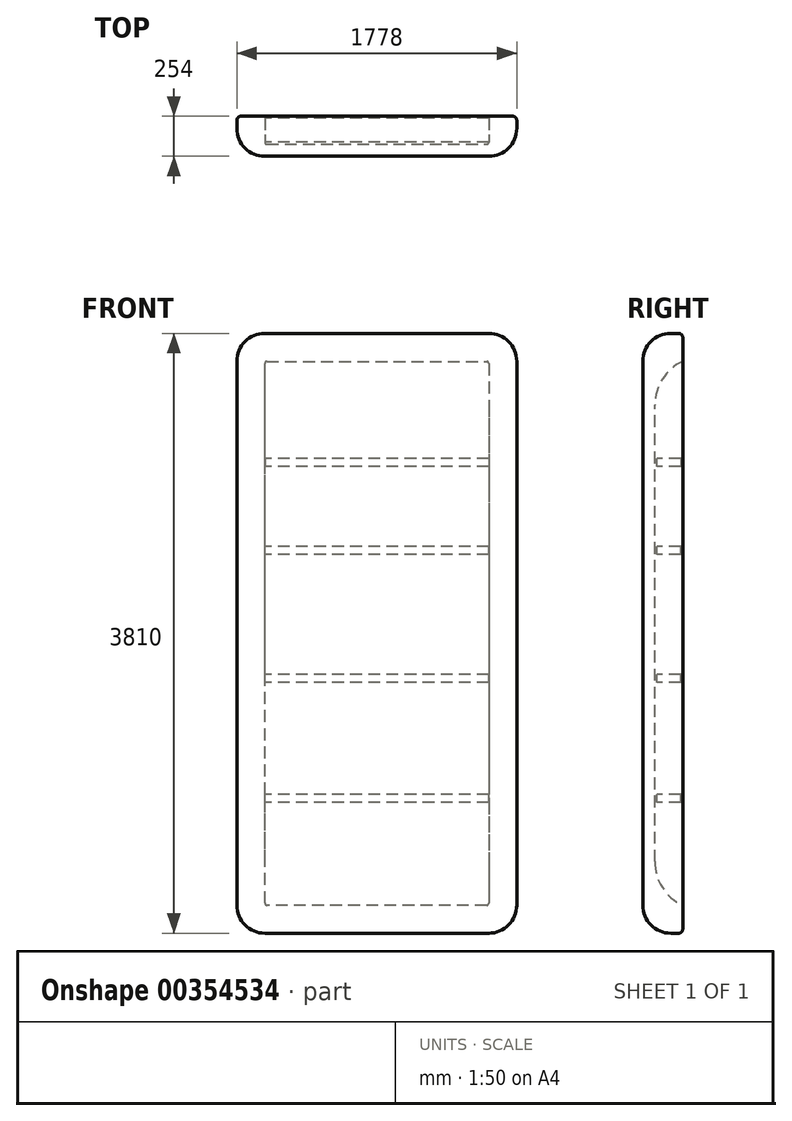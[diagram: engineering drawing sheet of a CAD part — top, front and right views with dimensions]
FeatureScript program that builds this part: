
annotation { "Feature Type Name" : "Feature", "Feature Type Description" : "" }
export const myFeature = defineFeature(function(context is Context, id is Id, definition is map)
    precondition{}
    {
        {
            var Q0;
            Q0=qCreatedBy(makeId("Front.planeOp"),FACE);
            var sketch = newSketch(context, id + "F0", { "sketchPlane" : qUnion([Q0])});
            skLineSegment(sketch, "E0.0", {"start": v(875.3, 1869.2) * mm, "end": v(-902.7, 1869.2) * mm});
            skLineSegment(sketch, "E0.1", {"start": v(875.3, -1940.8) * mm, "end": v(875.3, 1869.2) * mm});
            skLineSegment(sketch, "E0.2", {"start": v(-902.7, -1940.8) * mm, "end": v(875.3, -1940.8) * mm});
            skLineSegment(sketch, "E0.3", {"start": v(-902.7, 1869.2) * mm, "end": v(-902.7, -1940.8) * mm});
            skSolve(sketch);
        }
        {
            var Q0;
            Q0=makeQuery(id+"F0.imprint","IMPRINT",FACE,{"disambiguationData":[TD([[makeQuery(id+"F0.imprint","IMPRINT",EDGE,{"derivedFrom":sQuery(id+"F0.wireOp",EDGE,"E0.0")}),1.0]])]});
            extrude(context, id + "F1", {"entities" : qUnion([Q0]), "depth" : 254 * mm});
        }
        {
            var Q0;
            Q0=makeQuery(id+"F1.opExtrude","CAP_FACE",FACE,{"disambiguationData":[OSD([sQuery(id+"F0.wireOp",EDGE,"E0.0"),sQuery(id+"F0.wireOp",EDGE,"E0.1"),sQuery(id+"F0.wireOp",EDGE,"E0.2"),sQuery(id+"F0.wireOp",EDGE,"E0.3")])],"isStart":true});
            var sketch = newSketch(context, id + "F2", { "sketchPlane" : qUnion([Q0])});
            skLineSegment(sketch, "E1.0", {"start": v(724.9, 1691.4) * mm, "end": v(-697.5, 1691.4) * mm});
            skLineSegment(sketch, "E1.1", {"start": v(724.9, -1763) * mm, "end": v(724.9, 1691.4) * mm});
            skLineSegment(sketch, "E1.2", {"start": v(-697.5, -1763) * mm, "end": v(724.9, -1763) * mm});
            skLineSegment(sketch, "E1.3", {"start": v(-697.5, 1691.4) * mm, "end": v(-697.5, -1763) * mm});
            skSolve(sketch);
        }
        {
            var Q0;
            Q0=makeQuery(id+"F2.imprint","IMPRINT",FACE,{"disambiguationData":[TD([[makeQuery(id+"F2.imprint","IMPRINT",EDGE,{"derivedFrom":sQuery(id+"F2.wireOp",EDGE,"E1.0")}),1.0]])]});
            extrude(context, id + "F3", {"entities" : qUnion([Q0]), "operationType" : NewBodyOperationType.REMOVE, "oppositeDirection" : true, "depth" : 177.8 * mm});
        }
        {
            var Q0;
            Q0=makeQuery(id+"F1.opExtrude","CAP_FACE",FACE,{"disambiguationData":[OSD([sQuery(id+"F0.wireOp",EDGE,"E0.0"),sQuery(id+"F0.wireOp",EDGE,"E0.1"),sQuery(id+"F0.wireOp",EDGE,"E0.2"),sQuery(id+"F0.wireOp",EDGE,"E0.3")])],"isStart":false});
            var Q1;
            Q1=makeQuery(id+"F1.opExtrude","SWEPT_EDGE",EDGE,{"disambiguationData":[OSD([sQuery(id+"F0.wireOp",EDGE,"E0.0"),sQuery(id+"F0.wireOp",EDGE,"E0.3")])]});
            var Q2;
            Q2=makeQuery(id+"F1.opExtrude","SWEPT_EDGE",EDGE,{"disambiguationData":[OSD([sQuery(id+"F0.wireOp",EDGE,"E0.0"),sQuery(id+"F0.wireOp",EDGE,"E0.1")])]});
            var Q3;
            Q3=makeQuery(id+"F1.opExtrude","SWEPT_EDGE",EDGE,{"disambiguationData":[OSD([sQuery(id+"F0.wireOp",EDGE,"E0.2"),sQuery(id+"F0.wireOp",EDGE,"E0.3")])]});
            var Q4;
            Q4=makeQuery(id+"F1.opExtrude","SWEPT_EDGE",EDGE,{"disambiguationData":[OSD([sQuery(id+"F0.wireOp",EDGE,"E0.1"),sQuery(id+"F0.wireOp",EDGE,"E0.2")])]});
            fillet(context, id + "F4", {"entities" : qUnion([Q0, Q1, Q2, Q3, Q4]), "radius" : 177.8 * mm, "tangentPropagation" : true, "allowEdgeOverflow" : false});
        }
        {
            var Q0;
            Q0=makeQuery(id+"F3.boolean.opBoolean","COPY",EDGE,{"derivedFrom":makeQuery(id+"F3.opExtrude","CAP_EDGE",EDGE,{"disambiguationData":[OSD([sQuery(id+"F2.wireOp",EDGE,"E1.0")])],"isStart":false})});
            var Q1;
            Q1=makeQuery(id+"F3.boolean.opBoolean","COPY",EDGE,{"derivedFrom":makeQuery(id+"F3.opExtrude","CAP_EDGE",EDGE,{"disambiguationData":[OSD([sQuery(id+"F2.wireOp",EDGE,"E1.2")])],"isStart":false})});
            fillet(context, id + "F5", {"entities" : qUnion([Q0, Q1]), "radius" : 304.8 * mm, "tangentPropagation" : true, "allowEdgeOverflow" : false});
        }
        {
            var Q0;
            Q0=makeQuery(id+"F3.boolean.opBoolean","COPY",EDGE,{"derivedFrom":makeQuery(id+"F3.opExtrude","CAP_EDGE",EDGE,{"disambiguationData":[OSD([sQuery(id+"F2.wireOp",EDGE,"E1.1")])],"isStart":true})});
            var Q1;
            Q1=makeQuery(id+"F3.boolean.opBoolean","COPY",EDGE,{"derivedFrom":makeQuery(id+"F3.opExtrude","CAP_EDGE",EDGE,{"disambiguationData":[OSD([sQuery(id+"F2.wireOp",EDGE,"E1.3")])],"isStart":true})});
            var Q2;
            Q2=makeQuery(id+"F3.boolean.opBoolean","COPY",EDGE,{"derivedFrom":makeQuery(id+"F3.opExtrude","CAP_EDGE",EDGE,{"disambiguationData":[OSD([sQuery(id+"F2.wireOp",EDGE,"E1.3")])],"isStart":false})});
            var Q3;
            Q3=makeQuery(id+"F3.boolean.opBoolean","COPY",EDGE,{"derivedFrom":makeQuery(id+"F3.opExtrude","CAP_EDGE",EDGE,{"disambiguationData":[OSD([sQuery(id+"F2.wireOp",EDGE,"E1.1")])],"isStart":false})});
            fillet(context, id + "F6", {"entities" : qUnion([Q0, Q1, Q2, Q3]), "radius" : 12.7 * mm, "tangentPropagation" : true, "allowEdgeOverflow" : false});
        }
        {
            var Q0;
            Q0=makeQuery(id+"F1.opExtrude","CAP_EDGE",EDGE,{"disambiguationData":[OSD([sQuery(id+"F0.wireOp",EDGE,"E0.0")])],"isStart":true});
            fillet(context, id + "F7", {"entities" : qUnion([Q0]), "radius" : 25.4 * mm, "tangentPropagation" : true, "allowEdgeOverflow" : false});
        }
        {
            var Q0;
            Q0=makeQuery(id+"F3.boolean.opBoolean","COPY",FACE,{"derivedFrom":makeQuery(id+"F3.opExtrude","SWEPT_FACE",FACE,{"disambiguationData":[OSD([sQuery(id+"F2.wireOp",EDGE,"E1.1")])]})});
            var sketch = newSketch(context, id + "F8", { "sketchPlane" : qUnion([Q0])});
            skLineSegment(sketch, "E2.bottom", {"start": v(-12.7, -1110.64) * mm, "end": v(-165.1, -1110.64) * mm});
            skLineSegment(sketch, "E2.top", {"start": v(-12.7, -1059.84) * mm, "end": v(-165.1, -1059.84) * mm});
            skLineSegment(sketch, "E2.left", {"start": v(-12.7, -1110.64) * mm, "end": v(-12.7, -1059.84) * mm});
            skLineSegment(sketch, "E2.right", {"start": v(-165.1, -1110.64) * mm, "end": v(-165.1, -1059.84) * mm});
            skLineSegment(sketch, "E3.bottom", {"start": v(-12.7, -348.64) * mm, "end": v(-165.1, -348.64) * mm});
            skLineSegment(sketch, "E3.top", {"start": v(-12.7, -297.84) * mm, "end": v(-165.1, -297.84) * mm});
            skLineSegment(sketch, "E3.left", {"start": v(-12.7, -348.64) * mm, "end": v(-12.7, -297.84) * mm});
            skLineSegment(sketch, "E3.right", {"start": v(-165.1, -348.64) * mm, "end": v(-165.1, -297.84) * mm});
            skLineSegment(sketch, "E4.bottom", {"start": v(-12.7, 464.16) * mm, "end": v(-165.1, 464.16) * mm});
            skLineSegment(sketch, "E4.top", {"start": v(-12.7, 514.96) * mm, "end": v(-165.1, 514.96) * mm});
            skLineSegment(sketch, "E4.left", {"start": v(-12.7, 464.16) * mm, "end": v(-12.7, 514.96) * mm});
            skLineSegment(sketch, "E4.right", {"start": v(-165.1, 464.16) * mm, "end": v(-165.1, 514.96) * mm});
            skLineSegment(sketch, "E5.bottom", {"start": v(-12.7, 1073.76) * mm, "end": v(-165.1, 1073.76) * mm});
            skLineSegment(sketch, "E5.top", {"start": v(-12.7, 1022.96) * mm, "end": v(-165.1, 1022.96) * mm});
            skLineSegment(sketch, "E5.left", {"start": v(-12.7, 1073.76) * mm, "end": v(-12.7, 1022.96) * mm});
            skLineSegment(sketch, "E5.right", {"start": v(-165.1, 1073.76) * mm, "end": v(-165.1, 1022.96) * mm});
            skSolve(sketch);
        }
        {
            var Q0;
            Q0=makeQuery(id+"F8.imprint","IMPRINT",FACE,{"disambiguationData":[TD([[makeQuery(id+"F8.imprint","IMPRINT",EDGE,{"derivedFrom":sQuery(id+"F8.wireOp",EDGE,"E5.bottom")}),1.0]])]});
            var Q1;
            Q1=makeQuery(id+"F8.imprint","IMPRINT",FACE,{"disambiguationData":[TD([[makeQuery(id+"F8.imprint","IMPRINT",EDGE,{"derivedFrom":sQuery(id+"F8.wireOp",EDGE,"E4.bottom")}),-1.0]])]});
            var Q2;
            Q2=makeQuery(id+"F8.imprint","IMPRINT",FACE,{"disambiguationData":[TD([[makeQuery(id+"F8.imprint","IMPRINT",EDGE,{"derivedFrom":sQuery(id+"F8.wireOp",EDGE,"E3.bottom")}),-1.0]])]});
            var Q3;
            Q3=makeQuery(id+"F8.imprint","IMPRINT",FACE,{"disambiguationData":[TD([[makeQuery(id+"F8.imprint","IMPRINT",EDGE,{"derivedFrom":sQuery(id+"F8.wireOp",EDGE,"E2.bottom")}),-1.0]])]});
            extrude(context, id + "F9", {"entities" : qUnion([Q0, Q1, Q2, Q3]), "operationType" : NewBodyOperationType.ADD, "endBound" : BoundingType.UP_TO_NEXT, "depth" : 25.4 * mm});
        }
    });
